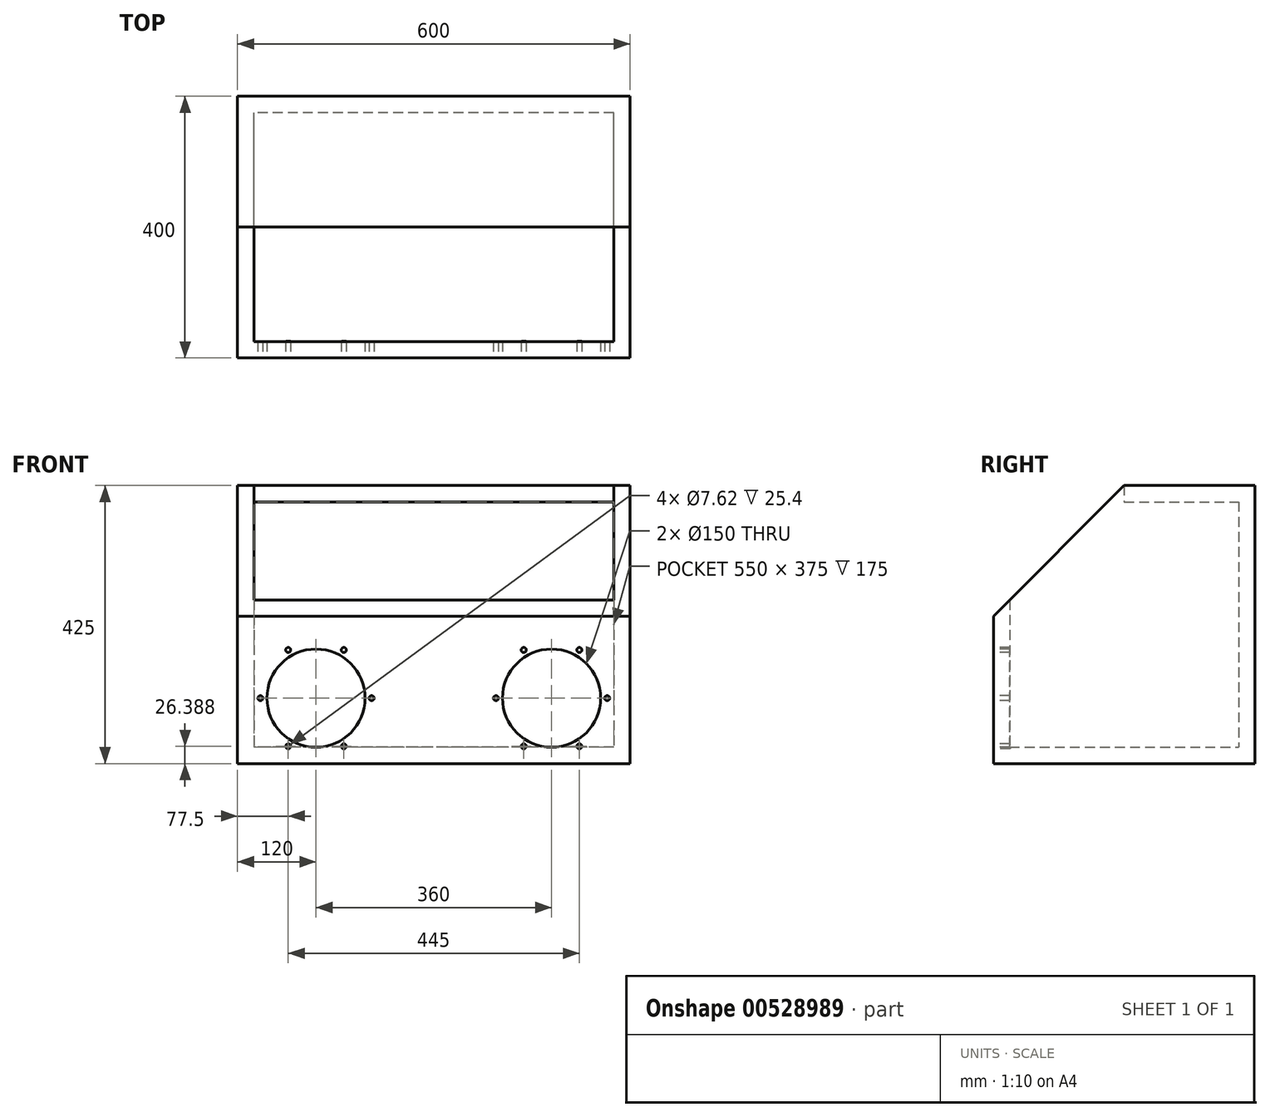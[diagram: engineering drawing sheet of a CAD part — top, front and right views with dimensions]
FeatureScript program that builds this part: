
annotation { "Feature Type Name" : "Feature", "Feature Type Description" : "" }
export const myFeature = defineFeature(function(context is Context, id is Id, definition is map)
    precondition{}
    {
        {
            var Q0;
            Q0=qCreatedBy(makeId("Top.planeOp"),FACE);
            var sketch = newSketch(context, id + "F0", { "sketchPlane" : qUnion([Q0])});
            skLineSegment(sketch, "E0.bottom", {"start": v(300, -200) * mm, "end": v(-300, -200) * mm});
            skLineSegment(sketch, "E0.top", {"start": v(300, 200) * mm, "end": v(-300, 200) * mm});
            skLineSegment(sketch, "E0.left", {"start": v(300, -200) * mm, "end": v(300, 200) * mm});
            skLineSegment(sketch, "E0.right", {"start": v(-300, -200) * mm, "end": v(-300, 200) * mm});
            skPoint(sketch, "E0.middle", {"position": v(0, 0) * mm});
            skSolve(sketch);
        }
        {
            var Q0;
            Q0 = qSketchRegion(id + "F0", true);
            extrude(context, id + "F1", {"entities" : qUnion([Q0]), "depth" : 25 * mm, "offsetDistance" : 25.4 * mm});
        }
        {
            var Q0;
            Q0=makeQuery(id+"F1.opExtrude","CAP_FACE",FACE,{"disambiguationData":[OSD([sQuery(id+"F0.wireOp",EDGE,"E0.bottom"),sQuery(id+"F0.wireOp",EDGE,"E0.top"),sQuery(id+"F0.wireOp",EDGE,"E0.left"),sQuery(id+"F0.wireOp",EDGE,"E0.right")])],"isStart":false});
            var sketch = newSketch(context, id + "F2", { "sketchPlane" : qUnion([Q0])});
            skLineSegment(sketch, "E1.bottom", {"start": v(300, -200) * mm, "end": v(-300, -200) * mm});
            skLineSegment(sketch, "E1.top", {"start": v(300, 200) * mm, "end": v(-300, 200) * mm});
            skLineSegment(sketch, "E1.left", {"start": v(300, -200) * mm, "end": v(300, 200) * mm});
            skLineSegment(sketch, "E1.right", {"start": v(-300, -200) * mm, "end": v(-300, 200) * mm});
            skPoint(sketch, "E1.middle", {"position": v(0, 0) * mm});
            skLineSegment(sketch, "E2.bottom", {"start": v(275, -175) * mm, "end": v(-275, -175) * mm});
            skLineSegment(sketch, "E2.top", {"start": v(275, 175) * mm, "end": v(-275, 175) * mm});
            skLineSegment(sketch, "E2.left", {"start": v(275, -175) * mm, "end": v(275, 175) * mm});
            skLineSegment(sketch, "E2.right", {"start": v(-275, -175) * mm, "end": v(-275, 175) * mm});
            skSolve(sketch);
        }
        {
            var Q0;
            Q0 = qSketchRegion(id + "F2", true);
            extrude(context, id + "F3", {"entities" : qUnion([Q0]), "operationType" : NewBodyOperationType.ADD, "depth" : 400 * mm, "offsetDistance" : 25.4 * mm});
        }
        {
            var Q0;
            Q0=makeQuery(id+"F3.boolean.opBoolean","MERGE",FACE,{"derivedFrom":[makeQuery(id+"F1.opExtrude","SWEPT_FACE",FACE,{"disambiguationData":[OSD([sQuery(id+"F0.wireOp",EDGE,"E0.right")])]}),makeQuery(id+"F3.opExtrude","SWEPT_FACE",FACE,{"disambiguationData":[OSD([sQuery(id+"F2.wireOp",EDGE,"E1.right")])]})]});
            var sketch = newSketch(context, id + "F4", { "sketchPlane" : qUnion([Q0])});
            skLineSegment(sketch, "E3", {"start": v(200, 425) * mm, "end": v(0, 425) * mm});
            skLineSegment(sketch, "E4", {"start": v(0, 425) * mm, "end": v(200, 225) * mm});
            skLineSegment(sketch, "E5", {"start": v(200, 225) * mm, "end": v(200, 425) * mm});
            skSolve(sketch);
        }
        {
            var Q0;
            Q0 = qSketchRegion(id + "F4", true);
            extrude(context, id + "F5", {"entities" : qUnion([Q0]), "operationType" : NewBodyOperationType.REMOVE, "endBound" : BoundingType.THROUGH_ALL, "oppositeDirection" : true, "depth" : 25.4 * mm, "offsetDistance" : 25.4 * mm});
        }
        {
            var Q0;
            Q0=makeQuery(id+"F3.opExtrude","CAP_FACE",FACE,{"disambiguationData":[OSD([sQuery(id+"F2.wireOp",EDGE,"E1.bottom"),sQuery(id+"F2.wireOp",EDGE,"E1.top"),sQuery(id+"F2.wireOp",EDGE,"E1.left"),sQuery(id+"F2.wireOp",EDGE,"E1.right"),sQuery(id+"F2.wireOp",EDGE,"E2.bottom"),sQuery(id+"F2.wireOp",EDGE,"E2.top"),sQuery(id+"F2.wireOp",EDGE,"E2.left"),sQuery(id+"F2.wireOp",EDGE,"E2.right")])],"isStart":false});
            var sketch = newSketch(context, id + "F6", { "sketchPlane" : qUnion([Q0])});
            skLineSegment(sketch, "E6.bottom", {"start": v(-300, 200) * mm, "end": v(300, 200) * mm});
            skLineSegment(sketch, "E6.top", {"start": v(-300, 0) * mm, "end": v(300, 0) * mm});
            skLineSegment(sketch, "E6.left", {"start": v(-300, 200) * mm, "end": v(-300, 0) * mm});
            skLineSegment(sketch, "E6.right", {"start": v(300, 200) * mm, "end": v(300, 0) * mm});
            skSolve(sketch);
        }
        {
            var Q0;
            Q0 = qSketchRegion(id + "F6", true);
            extrude(context, id + "F7", {"entities" : qUnion([Q0]), "operationType" : NewBodyOperationType.ADD, "oppositeDirection" : true, "depth" : 25 * mm, "offsetDistance" : 25.4 * mm});
        }
        {
            var Q0;
            Q0=makeQuery(id+"F3.boolean.opBoolean","MERGE",FACE,{"derivedFrom":[makeQuery(id+"F1.opExtrude","SWEPT_FACE",FACE,{"disambiguationData":[OSD([sQuery(id+"F0.wireOp",EDGE,"E0.bottom")])]}),makeQuery(id+"F3.opExtrude","SWEPT_FACE",FACE,{"disambiguationData":[OSD([sQuery(id+"F2.wireOp",EDGE,"E1.bottom")])]})]});
            var sketch = newSketch(context, id + "F8", { "sketchPlane" : qUnion([Q0])});
            skCircle(sketch, "E7", {"center": v(-180, 100) * mm, "radius": 75 * mm});
            skCircle(sketch, "E8", {"center": v(180, 100) * mm, "radius": 75 * mm});
            skCircle(sketch, "E9", {"center": v(-95, 100) * mm, "radius": 3.81 * mm});
            skCircle(sketch, "E10.1.0", {"center": v(-137.5, 173.61) * mm, "radius": 3.81 * mm});
            skCircle(sketch, "E10.2.0", {"center": v(-222.5, 173.61) * mm, "radius": 3.81 * mm});
            skCircle(sketch, "E10.3.0", {"center": v(-265, 100) * mm, "radius": 3.81 * mm});
            skCircle(sketch, "E10.4.0", {"center": v(-222.5, 26.39) * mm, "radius": 3.81 * mm});
            skCircle(sketch, "E10.5.0", {"center": v(-137.5, 26.39) * mm, "radius": 3.81 * mm});
            skCircle(sketch, "E11", {"center": v(95, 100) * mm, "radius": 3.81 * mm});
            skCircle(sketch, "E12.1.0", {"center": v(137.5, 26.39) * mm, "radius": 3.81 * mm});
            skCircle(sketch, "E12.2.0", {"center": v(222.5, 26.39) * mm, "radius": 3.81 * mm});
            skCircle(sketch, "E12.3.0", {"center": v(265, 100) * mm, "radius": 3.81 * mm});
            skCircle(sketch, "E12.4.0", {"center": v(222.5, 173.61) * mm, "radius": 3.81 * mm});
            skCircle(sketch, "E12.5.0", {"center": v(137.5, 173.61) * mm, "radius": 3.81 * mm});
            skSolve(sketch);
        }
        {
            var Q0;
            Q0 = qSketchRegion(id + "F8", true);
            extrude(context, id + "F9", {"entities" : qUnion([Q0]), "operationType" : NewBodyOperationType.REMOVE, "oppositeDirection" : true, "depth" : 25.4 * mm, "offsetDistance" : 25.4 * mm});
        }
        {
            var Q0;
            Q0 = qSketchRegion(id + "F8", true);
            extrude(context, id + "F10", {"entities" : qUnion([Q0]), "operationType" : NewBodyOperationType.REMOVE, "oppositeDirection" : true, "depth" : 25.4 * mm, "offsetDistance" : 25.4 * mm});
        }
    });
